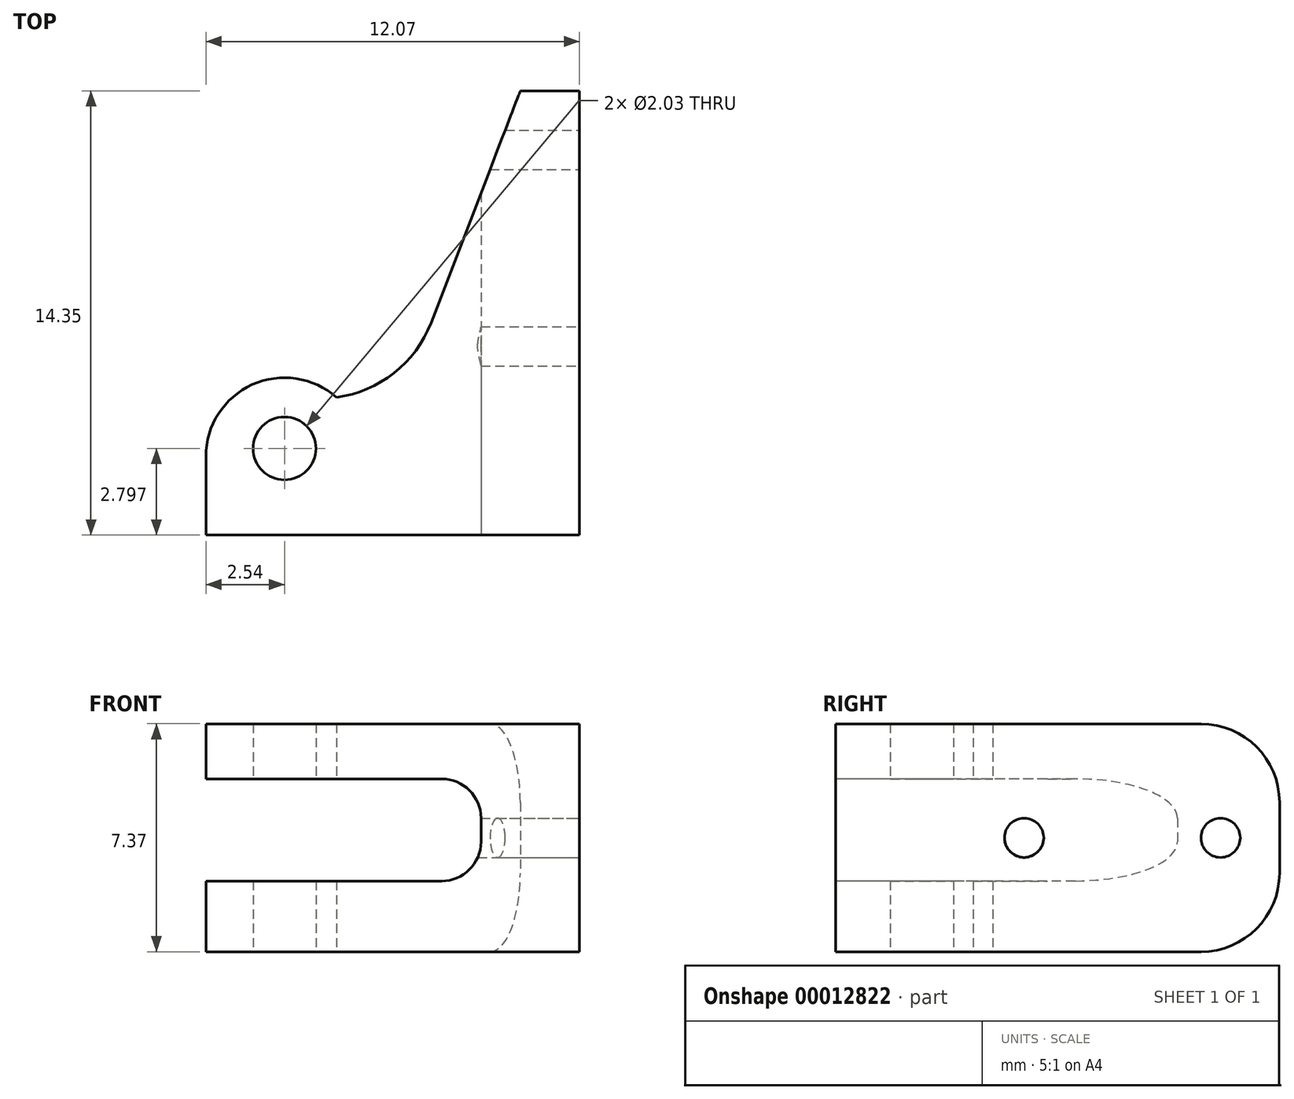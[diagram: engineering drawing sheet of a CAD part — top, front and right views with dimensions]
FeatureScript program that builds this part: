
annotation { "Feature Type Name" : "Feature", "Feature Type Description" : "" }
export const myFeature = defineFeature(function(context is Context, id is Id, definition is map)
    precondition{}
    {
        {
            var Q0;
            Q0=qCreatedBy(makeId("Top.planeOp"),FACE);
            var sketch = newSketch(context, id + "F0", { "sketchPlane" : qUnion([Q0])});
            skPoint(sketch, "E0.start.orphan", {"position": v(0, 4.76) * mm});
            skPoint(sketch, "E1.start.orphan", {"position": v(0, -4.76) * mm});
            skLineSegment(sketch, "E2.0.MirrorCS", {"start": v(9.53, 8.95) * mm, "end": v(9.52, -5.4) * mm});
            skPoint(sketch, "E3.end.orphan", {"position": v(8.9, 7.05) * mm});
            skLineSegment(sketch, "E4", {"start": v(9.52, 8.95) * mm, "end": v(7.62, 8.95) * mm});
            skPoint(sketch, "E5.orphan", {"position": v(10.16, 7.81) * mm});
            skLineSegment(sketch, "E6", {"start": v(1.68, -0.95) * mm, "end": v(3.8, -0.95) * mm});
            skPoint(sketch, "E7.start.orphan", {"position": v(10.16, 5.9) * mm});
            skPoint(sketch, "E8.start.orphan", {"position": v(10.16, 2.73) * mm});
            skPoint(sketch, "E9.orphan", {"position": v(0, 2.73) * mm});
            skPoint(sketch, "E10.start.orphan", {"position": v(0, 5.9) * mm});
            skLineSegment(sketch, "E11", {"start": v(7.62, 8.95) * mm, "end": v(3.81, -0.95) * mm});
            skCircle(sketch, "E12", {"center": v(0, -2.6) * mm, "radius": 1.02 * mm});
            skArc(sketch, "E13", {"start": v(1.68, -0.95) * mm, "mid": v(-1.05, -0.54) * mm, "end": v(-2.54, -2.86) * mm});
            skLineSegment(sketch, "E14", {"start": v(-2.54, -5.4) * mm, "end": v(9.52, -5.4) * mm});
            skLineSegment(sketch, "E15", {"start": v(-2.54, -2.86) * mm, "end": v(-2.54, -5.4) * mm});
            skPoint(sketch, "E16.orphan", {"position": v(0, -5.4) * mm});
            skPoint(sketch, "E17.start.orphan", {"position": v(0, -0.95) * mm});
            skPoint(sketch, "E18.orphan", {"position": v(-2.54, -4.76) * mm});
            skPoint(sketch, "E19.end.orphan", {"position": v(9.53, -4.76) * mm});
            skPoint(sketch, "E19.start.orphan", {"position": v(8.26, -4.76) * mm});
            skPoint(sketch, "E20.orphan", {"position": v(9.53, 0) * mm});
            skPoint(sketch, "E21.end.orphan", {"position": v(9.53, -0.32) * mm});
            skPoint(sketch, "E22.end.orphan", {"position": v(10.8, -0.95) * mm});
            skPoint(sketch, "E23.end.orphan", {"position": v(10.8, -4.76) * mm});
            skPoint(sketch, "E23.start.orphan", {"position": v(10.8, -5.4) * mm});
            skSolve(sketch);
        }
        {
            var Q0;
            Q0=qSketchRegion(id+"F0",true);
            extrude(context, id + "F1", {"entities" : qUnion([Q0]), "depth" : 7.37 * mm, "offsetDistance" : 25.4 * mm});
        }
        {
            var Q0;
            Q0=makeQuery(id+"F1.opExtrude","SWEPT_EDGE",EDGE,{"disambiguationData":[OSD([sQuery(id+"F0.wireOp",EDGE,"E6"),sQuery(id+"F0.wireOp",EDGE,"E11")])]});
            var Q1;
            Q1=makeQuery(id+"F1.opExtrude","SWEPT_EDGE",EDGE,{"disambiguationData":[OSD([sQuery(id+"F0.wireOp",EDGE,"E6"),sQuery(id+"F0.wireOp",EDGE,"E11")])]});
            fillet(context, id + "F2", {"entities" : qUnion([Q0, Q1]), "radius" : 3.8 * mm, "tangentPropagation" : true, "defaultsChanged" : false, "vertexSettings" : [], "allowEdgeOverflow" : false});
        }
        {
            var Q0;
            Q0=makeQuery(id+"F1.opExtrude","SWEPT_FACE",FACE,{"disambiguationData":[OSD([sQuery(id+"F0.wireOp",EDGE,"E14")])]});
            var sketch = newSketch(context, id + "F3", { "sketchPlane" : qUnion([Q0])});
            skLineSegment(sketch, "E24", {"start": v(-2.54, 5.59) * mm, "end": v(6.35, 5.59) * mm});
            skLineSegment(sketch, "E25", {"start": v(6.35, 5.59) * mm, "end": v(6.35, 2.29) * mm});
            skLineSegment(sketch, "E26", {"start": v(6.35, 2.29) * mm, "end": v(-2.54, 2.29) * mm});
            skSolve(sketch);
        }
        {
            var Q0;
            {var subQ2=sQuery(id+"F3.wireOp",EDGE,"E24");Q0=makeQuery(id+"F3.imprint","IMPRINT",FACE,{"disambiguationData":[TD([[makeQuery(id+"F3.imprint","IMPRINT",EDGE,{"derivedFrom":subQ2}),-1.0]])]});}
            extrude(context, id + "F4", {"entities" : qUnion([Q0]), "operationType" : NewBodyOperationType.REMOVE, "endBound" : BoundingType.THROUGH_ALL, "oppositeDirection" : true, "depth" : 25.4 * mm});
        }
        {
            var Q0;
            Q0=makeQuery(id+"F4.boolean.opBoolean","COPY",EDGE,{"derivedFrom":makeQuery(id+"F4.opExtrude","SWEPT_EDGE",EDGE,{"disambiguationData":[OSD([sQuery(id+"F3.wireOp",EDGE,"E24"),sQuery(id+"F3.wireOp",EDGE,"E25")])]})});
            var Q1;
            Q1=makeQuery(id+"F4.boolean.opBoolean","COPY",EDGE,{"derivedFrom":makeQuery(id+"F4.opExtrude","SWEPT_EDGE",EDGE,{"disambiguationData":[OSD([sQuery(id+"F3.wireOp",EDGE,"E25"),sQuery(id+"F3.wireOp",EDGE,"E26")])]})});
            var Q2;
            {var subQ0=sQuery(id+"F0.wireOp",EDGE,"E6");var subQ1=sQuery(id+"F0.wireOp",EDGE,"E13");Q2=makeQuery(id+"F4.boolean.opBoolean","SPLIT",EDGE,{"disambiguationData":[TD([makeQuery(id+"F4.opExtrude","SWEPT_FACE",FACE,{"disambiguationData":[OSD([sQuery(id+"F3.wireOp",EDGE,"E24")])]})])],"derivedFrom":makeQuery(id+"F1.opExtrude","SWEPT_EDGE",EDGE,{"disambiguationData":[OSD([subQ0,subQ1])]})});}
            var Q3;
            {var subQ0=sQuery(id+"F0.wireOp",EDGE,"E6");var subQ1=sQuery(id+"F0.wireOp",EDGE,"E13");Q3=makeQuery(id+"F4.boolean.opBoolean","SPLIT",EDGE,{"disambiguationData":[TD([makeQuery(id+"F4.opExtrude","SWEPT_FACE",FACE,{"disambiguationData":[OSD([sQuery(id+"F3.wireOp",EDGE,"E26")])]})])],"derivedFrom":makeQuery(id+"F1.opExtrude","SWEPT_EDGE",EDGE,{"disambiguationData":[OSD([subQ0,subQ1])]})});}
            fillet(context, id + "F5", {"entities" : qUnion([Q0, Q1, Q2, Q3]), "radius" : 1.27 * mm, "tangentPropagation" : true, "defaultsChanged" : false, "vertexSettings" : [], "allowEdgeOverflow" : false});
        }
        {
            var Q0;
            Q0=makeQuery(id+"F1.opExtrude","SWEPT_FACE",FACE,{"disambiguationData":[OSD([sQuery(id+"F0.wireOp",EDGE,"E2.0.MirrorCS")])]});
            var sketch = newSketch(context, id + "F6", { "sketchPlane" : qUnion([Q0])});
            skLineSegment(sketch, "E27", {"start": v(-5.4, 3.68) * mm, "end": v(8.95, 3.68) * mm, "construction": true});
            skCircle(sketch, "E28", {"center": v(0.7, 3.68) * mm, "radius": 0.64 * mm});
            skCircle(sketch, "E29", {"center": v(7.05, 3.68) * mm, "radius": 0.64 * mm});
            skSolve(sketch);
        }
        {
            var Q0;
            Q0=makeQuery(id+"F6.imprint","IMPRINT",FACE,{"disambiguationData":[TD([[makeQuery(id+"F6.imprint","IMPRINT",EDGE,{"derivedFrom":sQuery(id+"F6.wireOp",EDGE,"E28")}),1.0]])]});
            var Q1;
            Q1=makeQuery(id+"F6.imprint","IMPRINT",FACE,{"disambiguationData":[TD([[makeQuery(id+"F6.imprint","IMPRINT",EDGE,{"derivedFrom":sQuery(id+"F6.wireOp",EDGE,"E29")}),1.0]])]});
            var Q2;
            Q2=sQuery(id+"F6.wireOp",EDGE,"E28");
            var Q3;
            Q3=sQuery(id+"F6.wireOp",EDGE,"E29");
            extrude(context, id + "F7", {"entities" : qUnion([Q0, Q1]), "operationType" : NewBodyOperationType.REMOVE, "surfaceEntities" : qUnion([Q2, Q3]), "endBound" : BoundingType.THROUGH_ALL, "oppositeDirection" : true, "depth" : 25.4 * mm, "offsetDistance" : 25.4 * mm});
        }
        {
            var Q0;
            Q0=makeQuery(id+"F1.opExtrude","CAP_EDGE",EDGE,{"disambiguationData":[OSD([sQuery(id+"F0.wireOp",EDGE,"E4")])],"isStart":true});
            var Q1;
            Q1=makeQuery(id+"F1.opExtrude","CAP_EDGE",EDGE,{"disambiguationData":[OSD([sQuery(id+"F0.wireOp",EDGE,"E4")])],"isStart":false});
            fillet(context, id + "F8", {"entities" : qUnion([Q0, Q1]), "tangentPropagation" : true, "radius" : 2.54 * mm, "defaultsChanged" : false, "vertexSettings" : [], "allowEdgeOverflow" : false});
        }
    });
